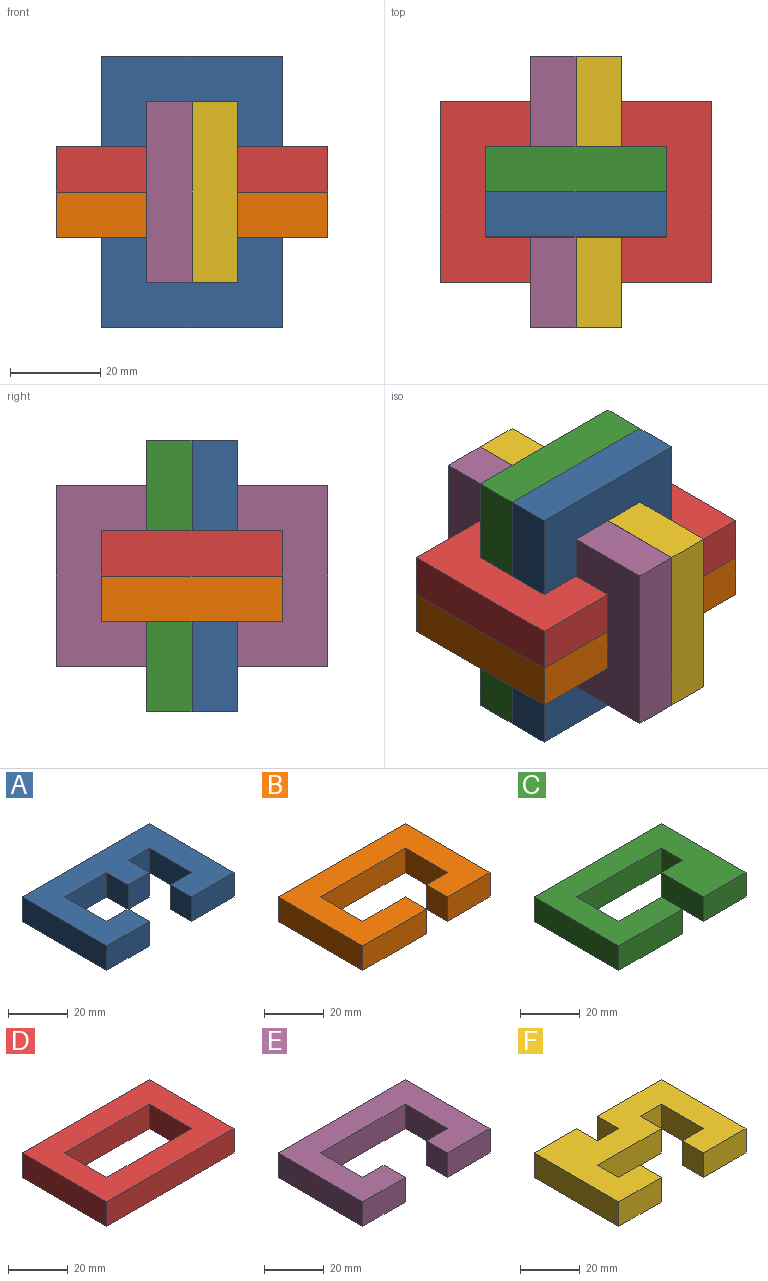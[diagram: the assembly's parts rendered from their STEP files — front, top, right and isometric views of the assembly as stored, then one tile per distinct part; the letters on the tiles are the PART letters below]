
ASSEMBLY  parts=6 mates=5
PART A: 18 faces, bbox 60x40x10 mm
  f0: plane 10x10mm, normal (0,1,0), area 100mm2, adj f1,f15,f16,f17
  f1: plane 20x10mm, normal (1,0,0), area 200mm2, adj f0,f2,f16,f17
  f2: plane 20x10mm, normal (0,-1,0), area 200mm2, adj f1,f3,f16,f17
  f3: plane 10x10mm, normal (-1,0,0), area 100mm2, adj f2,f4,f16,f17
  f4: plane 10x10mm, normal (0,-1,0), area 100mm2, adj f3,f5,f16,f17
  f5: plane 10x10mm, normal (1,0,0), area 100mm2, adj f4,f6,f16,f17
  f6: plane 10x10mm, normal (0,-1,0), area 100mm2, adj f5,f7,f16,f17
  f7: plane 20x10mm, normal (-1,0,0), area 200mm2, adj f6,f8,f16,f17
  f8: plane 10x10mm, normal (0,1,0), area 100mm2, adj f7,f9,f16,f17
  f9: plane 10x10mm, normal (-1,0,0), area 100mm2, adj f8,f10,f16,f17
  f10: plane 20x10mm, normal (0,-1,0), area 200mm2, adj f9,f11,f16,f17
  f11: plane 40x10mm, normal (1,0,0), area 400mm2, adj f10,f12,f16,f17
  f12: plane 60x10mm, normal (0,1,0), area 600mm2, adj f11,f13,f16,f17
  f13: plane 40x10mm, normal (-1,0,0), area 400mm2, adj f12,f14,f16,f17
  f14: plane 20x10mm, normal (0,-1,0), area 200mm2, adj f13,f15,f16,f17
  f15: plane 10x10mm, normal (1,0,0), area 100mm2, adj f0,f14,f16,f17
  f16: plane 60x40mm, normal (0,0,1), area 1500mm2, adj f0,f1,f2,f3,f4,f5,f6,f7
  f17: plane 60x40mm, normal (0,0,-1), area 1500mm2, adj f0,f1,f2,f3,f4,f5,f6,f7
PART B: 14 faces, bbox 60x40x10 mm
  f0: plane 20x10mm, normal (0,1,0), area 200mm2, adj f1,f11,f12,f13
  f1: plane 20x10mm, normal (1,0,0), area 200mm2, adj f0,f2,f12,f13
  f2: plane 40x10mm, normal (0,-1,0), area 400mm2, adj f1,f3,f12,f13
  f3: plane 20x10mm, normal (-1,0,0), area 200mm2, adj f2,f4,f12,f13
  f4: plane 10x10mm, normal (0,1,0), area 100mm2, adj f3,f5,f12,f13
  f5: plane 10x10mm, normal (-1,0,0), area 100mm2, adj f4,f6,f12,f13
  f6: plane 20x10mm, normal (0,-1,0), area 200mm2, adj f5,f7,f12,f13
  f7: plane 40x10mm, normal (1,0,0), area 400mm2, adj f6,f8,f12,f13
  f8: plane 60x10mm, normal (0,1,0), area 600mm2, adj f7,f9,f12,f13
  f9: plane 40x10mm, normal (-1,0,0), area 400mm2, adj f8,f10,f12,f13
  f10: plane 30x10mm, normal (0,-1,0), area 300mm2, adj f9,f11,f12,f13
  f11: plane 10x10mm, normal (1,0,0), area 100mm2, adj f0,f10,f12,f13
  f12: plane 60x40mm, normal (0,0,1), area 1500mm2, adj f0,f1,f2,f3,f4,f5,f6,f7
  f13: plane 60x40mm, normal (0,0,-1), area 1500mm2, adj f0,f1,f2,f3,f4,f5,f6,f7
PART C: 14 faces, bbox 60x40x10 mm
  f0: plane 20x10mm, normal (0,1,0), area 200mm2, adj f1,f11,f12,f13
  f1: plane 20x10mm, normal (1,0,0), area 200mm2, adj f0,f2,f12,f13
  f2: plane 40x10mm, normal (0,-1,0), area 400mm2, adj f1,f3,f12,f13
  f3: plane 10x10mm, normal (-1,0,0), area 100mm2, adj f2,f4,f12,f13
  f4: plane 10x10mm, normal (0,1,0), area 100mm2, adj f3,f5,f12,f13
  f5: plane 20x10mm, normal (-1,0,0), area 200mm2, adj f4,f6,f12,f13
  f6: plane 20x10mm, normal (0,-1,0), area 200mm2, adj f5,f7,f12,f13
  f7: plane 40x10mm, normal (1,0,0), area 400mm2, adj f6,f8,f12,f13
  f8: plane 60x10mm, normal (0,1,0), area 600mm2, adj f7,f9,f12,f13
  f9: plane 40x10mm, normal (-1,0,0), area 400mm2, adj f8,f10,f12,f13
  f10: plane 30x10mm, normal (0,-1,0), area 300mm2, adj f9,f11,f12,f13
  f11: plane 10x10mm, normal (1,0,0), area 100mm2, adj f0,f10,f12,f13
  f12: plane 60x40mm, normal (0,0,1), area 1600mm2, adj f0,f1,f2,f3,f4,f5,f6,f7
  f13: plane 60x40mm, normal (0,0,-1), area 1600mm2, adj f0,f1,f2,f3,f4,f5,f6,f7
PART D: 10 faces, bbox 60x40x10 mm
  f0: plane 40x10mm, normal (-1,0,0), area 400mm2, adj f1,f7,f8,f9
  f1: plane 60x10mm, normal (0,-1,0), area 600mm2, adj f0,f2,f8,f9
  f2: plane 40x10mm, normal (1,0,0), area 400mm2, adj f1,f7,f8,f9
  f3: plane 40x10mm, normal (0,1,0), area 400mm2, adj f4,f6,f8,f9
  f4: plane 20x10mm, normal (1,0,0), area 200mm2, adj f3,f5,f8,f9
  f5: plane 40x10mm, normal (0,-1,0), area 400mm2, adj f4,f6,f8,f9
  f6: plane 20x10mm, normal (-1,0,0), area 200mm2, adj f3,f5,f8,f9
  f7: plane 60x10mm, normal (0,1,0), area 600mm2, adj f0,f2,f8,f9
  f8: plane 60x40mm, normal (0,0,1), area 1600mm2, adj f0,f1,f2,f3,f4,f5,f6,f7
  f9: plane 60x40mm, normal (0,0,-1), area 1600mm2, adj f0,f1,f2,f3,f4,f5,f6,f7
PART E: 14 faces, bbox 60x40x10 mm
  f0: plane 10x10mm, normal (0,1,0), area 100mm2, adj f1,f11,f12,f13
  f1: plane 20x10mm, normal (1,0,0), area 200mm2, adj f0,f2,f12,f13
  f2: plane 40x10mm, normal (0,-1,0), area 400mm2, adj f1,f3,f12,f13
  f3: plane 20x10mm, normal (-1,0,0), area 200mm2, adj f2,f4,f12,f13
  f4: plane 10x10mm, normal (0,1,0), area 100mm2, adj f3,f5,f12,f13
  f5: plane 10x10mm, normal (-1,0,0), area 100mm2, adj f4,f6,f12,f13
  f6: plane 20x10mm, normal (0,-1,0), area 200mm2, adj f5,f7,f12,f13
  f7: plane 40x10mm, normal (1,0,0), area 400mm2, adj f6,f8,f12,f13
  f8: plane 60x10mm, normal (0,1,0), area 600mm2, adj f7,f9,f12,f13
  f9: plane 40x10mm, normal (-1,0,0), area 400mm2, adj f8,f10,f12,f13
  f10: plane 20x10mm, normal (0,-1,0), area 200mm2, adj f9,f11,f12,f13
  f11: plane 10x10mm, normal (1,0,0), area 100mm2, adj f0,f10,f12,f13
  f12: plane 60x40mm, normal (0,0,1), area 1400mm2, adj f0,f1,f2,f3,f4,f5,f6,f7
  f13: plane 60x40mm, normal (0,0,-1), area 1400mm2, adj f0,f1,f2,f3,f4,f5,f6,f7
PART F: 20 faces, bbox 60x40x10 mm
  f0: plane 10x10mm, normal (0,1,0), area 100mm2, adj f1,f17,f18,f19
  f1: plane 10x10mm, normal (1,0,0), area 100mm2, adj f0,f2,f18,f19
  f2: plane 20x10mm, normal (0,1,0), area 200mm2, adj f1,f3,f18,f19
  f3: plane 40x10mm, normal (-1,0,0), area 400mm2, adj f2,f4,f18,f19
  f4: plane 20x10mm, normal (0,-1,0), area 200mm2, adj f3,f5,f18,f19
  f5: plane 10x10mm, normal (1,0,0), area 100mm2, adj f4,f6,f18,f19
  f6: plane 10x10mm, normal (0,1,0), area 100mm2, adj f5,f7,f18,f19
  f7: plane 10x10mm, normal (1,0,0), area 100mm2, adj f6,f8,f18,f19
  f8: plane 30x10mm, normal (0,-1,0), area 300mm2, adj f7,f9,f18,f19
  f9: plane 10x10mm, normal (1,0,0), area 100mm2, adj f8,f10,f18,f19
  f10: plane 10x10mm, normal (0,-1,0), area 100mm2, adj f9,f11,f18,f19
  f11: plane 20x10mm, normal (-1,0,0), area 200mm2, adj f10,f12,f18,f19
  f12: plane 10x10mm, normal (0,1,0), area 100mm2, adj f11,f13,f18,f19
  f13: plane 10x10mm, normal (-1,0,0), area 100mm2, adj f12,f14,f18,f19
  f14: plane 20x10mm, normal (0,-1,0), area 200mm2, adj f13,f15,f18,f19
  f15: plane 40x10mm, normal (1,0,0), area 400mm2, adj f14,f16,f18,f19
  f16: plane 30x10mm, normal (0,1,0), area 300mm2, adj f15,f17,f18,f19
  f17: plane 10x10mm, normal (-1,0,0), area 100mm2, adj f0,f16,f18,f19
  f18: plane 60x40mm, normal (0,0,1), area 1600mm2, adj f0,f1,f2,f3,f4,f5,f6,f7
  f19: plane 60x40mm, normal (0,0,-1), area 1600mm2, adj f0,f1,f2,f3,f4,f5,f6,f7
PLACE A rot(axis=(0.58,0.58,-0.58),120deg) t=(-30,-20,0)mm
PLACE B t=(-30,-20,-10)mm
PLACE C rot(axis=(0.58,0.58,-0.58),120deg) t=(-30,-10,0)mm
PLACE D t=(-30,-20,0)mm
PLACE E rot(axis=(0.58,-0.58,-0.58),120deg) t=(-30,-20,0)mm
PLACE F rot(axis=(0.58,0.58,0.58),120deg) t=(-30,-20,0)mm
MATE fastened B.f12 <-> D.f9  axis (0,0,1) through (0,0,0)mm
MATE fastened D.f8 <-> E.f2  axis (0,0,1) through (-60,-40,10)mm
MATE fastened C.f12 <-> A.f17  axis (0,-1,0) through (-10,-20,-30)mm
MATE fastened F.f19 <-> E.f13  axis (-1,0,0) through (-30,-50,20)mm
MATE fastened A.f14 <-> D.f4  axis (-1,0,0) through (-50,-30,10)mm
